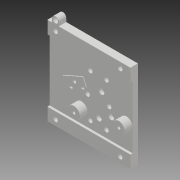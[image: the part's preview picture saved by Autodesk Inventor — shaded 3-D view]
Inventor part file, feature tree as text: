
AUTODESK INVENTOR PART (.ipt)
format: ipt  version: 2017.3 (Build 213257000, 257)  size: 288,768 bytes
history: native  units: mm
features: sketch x9, extrude x8, plane x5, hole x4, other x3, projected_geometry x3, chamfer x2
ambient origin geometry x8: Origin, YZ Plane, XZ Plane, XY Plane, X Axis, Y Axis, Z Axis, Center Point
bodies: Solid1 (feature_tree)
feature tree (34):
  extrude  "Extrusion1"  Depth=6.35mm TaperAngle=0.0deg
  other  "cp adapter placement"
  other  "grating mount placement"
  other  "post mount placement"
  plane  "Work Plane1"
  extrude  "CP support"  Depth=6.35mm TaperAngle=0.0deg
  plane  "Work Plane2"
  extrude  "post supports"  Depth=5.08mm
  plane  "Work Plane3"
  extrude  "grating support"  Depth=2.0mm TaperAngle=0.0deg
  hole  "Hole1"  [1 undecoded]
  hole  "Hole2"  [1 undecoded]
  hole  "Hole3"  [1 undecoded]
  extrude  "grating alignment"  Depth=2.0mm TaperAngle=45.0deg
  sketch  "Sketch10"  dims[d27=6.0mm d28=5.558mm d29=5.08mm d30=14.3117mm d31=8.0mm d32=20.594885mm d33=15.0mm]
  plane  "Work Plane4"
  extrude  "Extrusion6"  Depth=2.0mm
  sketch  "Sketch11"  dims[d34=3.0mm d35=2.0mm d36=0.0mm]
  plane  "Work Plane5"
  extrude  "Extrusion7"  Depth=2.0mm TaperAngle=45.0deg
  extrude  "Extrusion8"  [1 undecoded]
  hole  "Hole5"  [1 undecoded]
  chamfer  "top chamfer"  [1 undecoded]
  chamfer  "Chamfer2"  [1 undecoded]
  sketch  "Sketch1"  dims[d3=0.0mm d4=6.35mm d5=0.0mm]
  sketch  "Sketch5"  dims[d7=14.2mm d8=6.35mm d9=0.0mm]
  sketch  "Sketch7"  dims[d10=6.35mm d11=0.0mm]
  projected_geometry  "Projected Loop1"
  projected_geometry  "Projected Loop2"
  sketch  "Sketch8"  dims[d13=6.0mm d14=4.0mm d15=2.0mm d16=90.0deg d17=8.0mm d18=20.594885mm]
  sketch  "Sketch9"  dims[d19=3.264mm d20=6.0mm d21=5.558mm d22=5.08mm d23=14.3117mm d24=8.0mm d25=20.594885mm]
  sketch  "Sketch12"  dims[d37=0.0mm d38=0.0mm d39=2.0mm d40=0.0mm]
  sketch  "Sketch17"  dims[d41=2.0mm d42=0.0mm d51=5.1308mm d52=6.0mm d53=4.0mm d54=2.0mm d55=90.0deg d56=8.0mm d57=20.594885mm d59=19.05mm d61=2.0mm d62=45.0deg d63=0.2mm d64=2.0mm d65=45.0deg]
  projected_geometry  "Projected Loop3"
note: 7 required parameter values undecoded (feature->parameter linkage not recoverable at this tier; creation-order binding heuristic only, values carry confidence <= 0.55)
